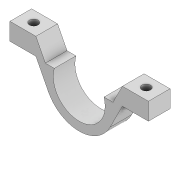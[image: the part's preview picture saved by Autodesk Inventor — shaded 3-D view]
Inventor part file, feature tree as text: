
AUTODESK INVENTOR PART (.ipt)
format: ipt  version: 2022 (Build 260153000, 153)  size: 128,512 bytes
history: native  units: mm
features: extrude x2, sketch x1
ambient origin geometry x8: Origin, YZ Plane, XZ Plane, XY Plane, X Axis, Y Axis, Z Axis, Center Point
bodies: Solid1 (feature_tree)
feature tree (3):
  extrude  "Extrusion1"  Depth=5.0mm
  extrude  "Extrusion4"  Depth=5.0mm
  sketch  "Sketch4"  dims[d5=5.0mm d6=0.0mm d12=12.0mm d13=2.0mm d14=16.0mm d15=16.0mm d16=6.0mm d17=4.0mm d18=6.0mm d19=4.0mm d20=1.0mm d21=1.0mm d39=13.0mm d40=13.0mm d41=2.0mm d42=2.0mm d43=3.0mm d44=3.0mm d45=2.5mm d46=2.5mm d47=5.0mm d48=0.0mm]
